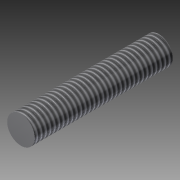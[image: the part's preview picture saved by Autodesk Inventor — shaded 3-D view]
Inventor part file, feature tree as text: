
AUTODESK INVENTOR PART (.ipt)
format: ipt  version: 2014 (Build 180170000, 170)  size: 80,896 bytes
history: native  units: mm
features: extrude x1, thread x1, sketch x1
ambient origin geometry x8: Origin, YZ Plane, XZ Plane, XY Plane, X Axis, Y Axis, Z Axis, Center Point
bodies: Solid1 (feature_tree)
feature tree (3):
  extrude  "Extrusion1"  Depth=25.0mm TaperAngle=0.0deg
  thread  "Thread1"  [1 undecoded]
  sketch  "Sketch1"  dims[d0=5.0mm d1=25.0mm d2=0.0mm d3=10.0mm d4=0.0mm]
note: 1 required parameter value undecoded (feature->parameter linkage not recoverable at this tier; creation-order binding heuristic only, values carry confidence <= 0.55)
